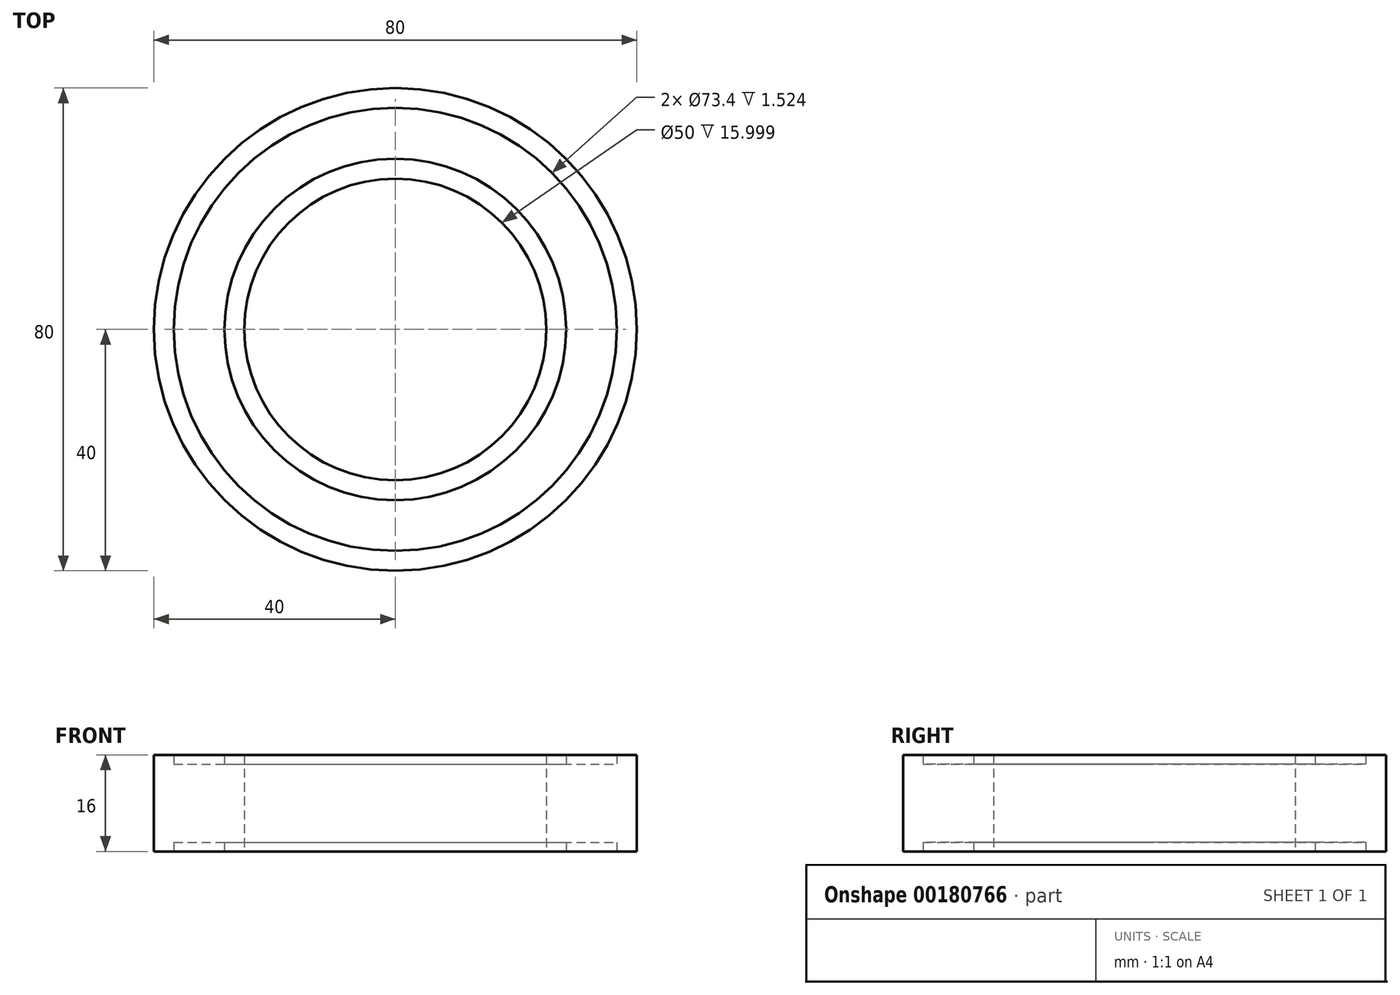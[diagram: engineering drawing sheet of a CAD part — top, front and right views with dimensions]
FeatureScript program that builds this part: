
annotation { "Feature Type Name" : "Feature", "Feature Type Description" : "" }
export const myFeature = defineFeature(function(context is Context, id is Id, definition is map)
    precondition{}
    {
        {
            var Q0;
            Q0=qCreatedBy(makeId("Right.planeOp"),FACE);
            var sketch = newSketch(context, id + "F0", { "sketchPlane" : qUnion([Q0])});
            skLineSegment(sketch, "E0", {"start": v(0, 0) * mm, "end": v(0, 16) * mm, "construction": true});
            skLineSegment(sketch, "E1", {"start": v(-25, 0) * mm, "end": v(-25, 16) * mm});
            skLineSegment(sketch, "E2", {"start": v(-25, 16) * mm, "end": v(-28.3, 16) * mm});
            skLineSegment(sketch, "E3", {"start": v(-28.3, 16) * mm, "end": v(-28.3, 14.48) * mm});
            skLineSegment(sketch, "E4", {"start": v(-28.3, 14.48) * mm, "end": v(-36.7, 14.48) * mm});
            skLineSegment(sketch, "E5", {"start": v(-36.7, 14.48) * mm, "end": v(-36.7, 16) * mm});
            skLineSegment(sketch, "E6", {"start": v(-36.7, 16) * mm, "end": v(-40, 16) * mm});
            skLineSegment(sketch, "E7", {"start": v(-40, 16) * mm, "end": v(-40, 0) * mm});
            skLineSegment(sketch, "E8", {"start": v(-40, 0) * mm, "end": v(-36.7, 0) * mm});
            skLineSegment(sketch, "E9", {"start": v(-36.7, 0) * mm, "end": v(-36.7, 1.52) * mm});
            skLineSegment(sketch, "E10", {"start": v(-36.7, 1.52) * mm, "end": v(-28.3, 1.52) * mm});
            skLineSegment(sketch, "E11", {"start": v(-28.3, 1.52) * mm, "end": v(-28.3, 0) * mm});
            skLineSegment(sketch, "E12", {"start": v(-28.3, 0) * mm, "end": v(-25, 0) * mm});
            skSolve(sketch);
        }
        {
            var Q0;
            Q0 = qSketchRegion(id + "F0", true);
            var Q1;
            Q1=sQuery(id+"F0.wireOp",EDGE,"E0");
            revolve(context, id + "F1", {"entities" : qUnion([Q0]), "axis" : qUnion([Q1]), "revolveType" : RevolveType.FULL});
        }
    });
